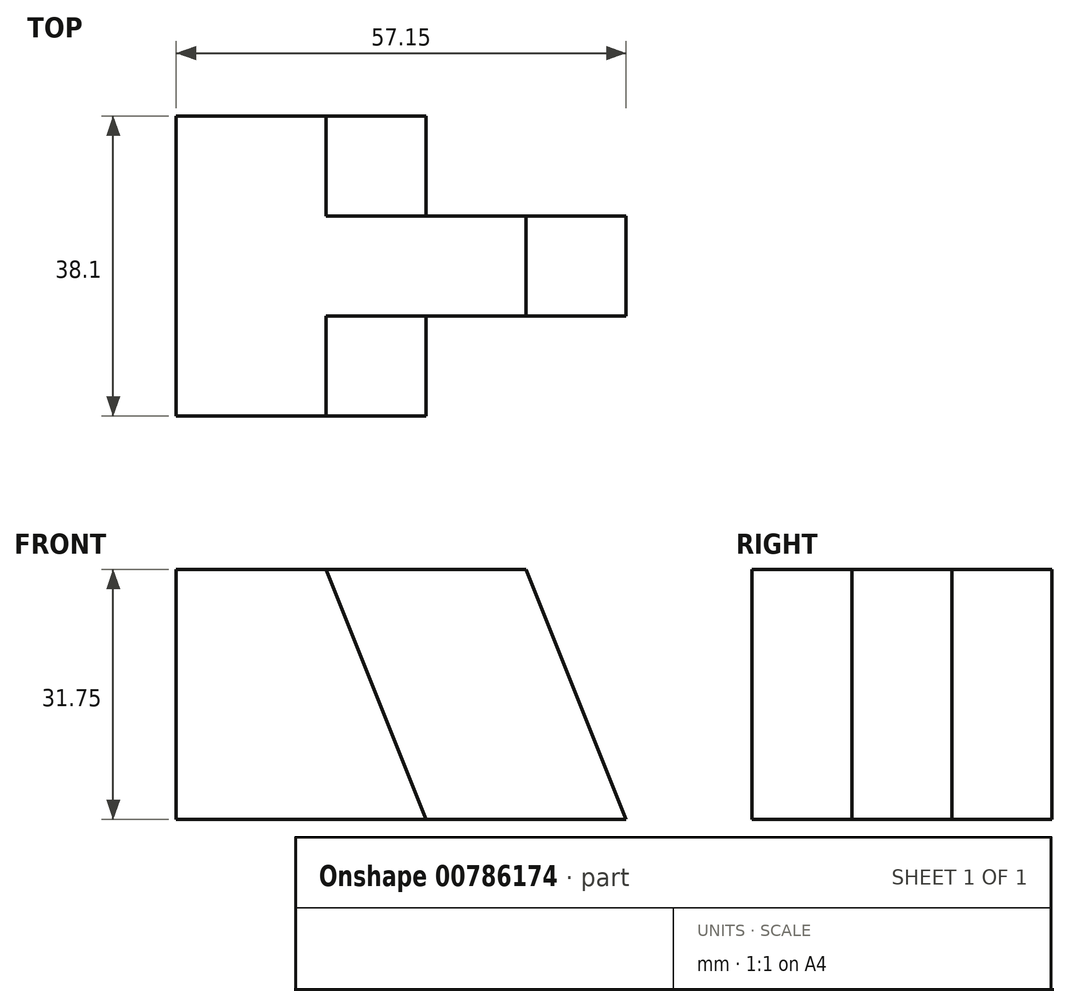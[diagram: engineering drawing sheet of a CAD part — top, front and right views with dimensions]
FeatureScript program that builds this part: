
annotation { "Feature Type Name" : "Feature", "Feature Type Description" : "" }
export const myFeature = defineFeature(function(context is Context, id is Id, definition is map)
    precondition{}
    {
        {
            var Q0;
            Q0=qCreatedBy(makeId("Front.planeOp"),FACE);
            var sketch = newSketch(context, id + "F0", { "sketchPlane" : qUnion([Q0])});
            skLineSegment(sketch, "E0", {"start": v(0, 0) * mm, "end": v(0, 31.75) * mm});
            skLineSegment(sketch, "E1", {"start": v(0, 0) * mm, "end": v(57.15, 0) * mm});
            skLineSegment(sketch, "E2", {"start": v(57.15, 0) * mm, "end": v(57.15, 31.75) * mm});
            skLineSegment(sketch, "E3", {"start": v(57.15, 31.75) * mm, "end": v(0, 31.75) * mm});
            skSolve(sketch);
        }
        {
            var Q0;
            Q0=makeQuery(id+"F0.imprint","IMPRINT",FACE,{"disambiguationData":[TD([[makeQuery(id+"F0.imprint","IMPRINT",EDGE,{"derivedFrom":sQuery(id+"F0.wireOp",EDGE,"E0")}),-1.0]])]});
            extrude(context, id + "F1", {"entities" : qUnion([Q0]), "depth" : 38.1 * mm, "offsetDistance" : 25.4 * mm});
        }
        {
            var Q0;
            Q0=makeQuery(id+"F1.opExtrude","CAP_FACE",FACE,{"disambiguationData":[OSD([sQuery(id+"F0.wireOp",EDGE,"E0"),sQuery(id+"F0.wireOp",EDGE,"E1"),sQuery(id+"F0.wireOp",EDGE,"E2"),sQuery(id+"F0.wireOp",EDGE,"E3")])],"isStart":false});
            var sketch = newSketch(context, id + "F2", { "sketchPlane" : qUnion([Q0])});
            skLineSegment(sketch, "E4", {"start": v(57.15, 31.75) * mm, "end": v(19.05, 31.75) * mm});
            skLineSegment(sketch, "E5", {"start": v(57.15, 31.75) * mm, "end": v(57.15, 0) * mm});
            skLineSegment(sketch, "E6", {"start": v(57.15, 0) * mm, "end": v(31.75, 0) * mm});
            skLineSegment(sketch, "E7", {"start": v(31.75, 0) * mm, "end": v(19.05, 31.75) * mm});
            skSolve(sketch);
        }
        {
            var Q0;
            Q0=makeQuery(id+"F2.imprint","IMPRINT",FACE,{"disambiguationData":[TD([[makeQuery(id+"F2.imprint","IMPRINT",EDGE,{"derivedFrom":sQuery(id+"F2.wireOp",EDGE,"E4")}),1.0]])]});
            extrude(context, id + "F3", {"entities" : qUnion([Q0]), "operationType" : NewBodyOperationType.REMOVE, "oppositeDirection" : true, "depth" : 12.7 * mm, "offsetDistance" : 25.4 * mm});
        }
        {
            var Q0;
            Q0=makeQuery(id+"F1.opExtrude","CAP_FACE",FACE,{"disambiguationData":[OSD([sQuery(id+"F0.wireOp",EDGE,"E0"),sQuery(id+"F0.wireOp",EDGE,"E1"),sQuery(id+"F0.wireOp",EDGE,"E2"),sQuery(id+"F0.wireOp",EDGE,"E3")])],"isStart":true});
            var sketch = newSketch(context, id + "F4", { "sketchPlane" : qUnion([Q0])});
            skLineSegment(sketch, "E8", {"start": v(-57.15, 31.75) * mm, "end": v(-19.05, 31.75) * mm});
            skLineSegment(sketch, "E9", {"start": v(-57.15, 31.75) * mm, "end": v(-57.15, 0) * mm});
            skLineSegment(sketch, "E10", {"start": v(-57.15, 0) * mm, "end": v(-31.75, 0) * mm});
            skLineSegment(sketch, "E11", {"start": v(-31.75, 0) * mm, "end": v(-19.05, 31.75) * mm});
            skSolve(sketch);
        }
        {
            var Q0;
            Q0=makeQuery(id+"F4.imprint","IMPRINT",FACE,{"disambiguationData":[TD([[makeQuery(id+"F4.imprint","IMPRINT",EDGE,{"derivedFrom":sQuery(id+"F4.wireOp",EDGE,"E8")}),-1.0]])]});
            extrude(context, id + "F5", {"entities" : qUnion([Q0]), "operationType" : NewBodyOperationType.REMOVE, "oppositeDirection" : true, "depth" : 12.7 * mm, "offsetDistance" : 25.4 * mm});
        }
        {
            var Q0;
            Q0=makeQuery(id+"F3.boolean.opBoolean","COPY",FACE,{"derivedFrom":makeQuery(id+"F3.opExtrude","CAP_FACE",FACE,{"disambiguationData":[OSD([sQuery(id+"F2.wireOp",EDGE,"E4"),sQuery(id+"F2.wireOp",EDGE,"E5"),sQuery(id+"F2.wireOp",EDGE,"E6"),sQuery(id+"F2.wireOp",EDGE,"E7")])],"isStart":false})});
            var sketch = newSketch(context, id + "F6", { "sketchPlane" : qUnion([Q0])});
            skLineSegment(sketch, "E12", {"start": v(57.15, 0) * mm, "end": v(57.15, 31.75) * mm});
            skLineSegment(sketch, "E13", {"start": v(57.15, 31.75) * mm, "end": v(44.45, 31.75) * mm});
            skLineSegment(sketch, "E14", {"start": v(44.45, 31.75) * mm, "end": v(57.15, 0) * mm});
            skSolve(sketch);
        }
        {
            var Q0;
            Q0=makeQuery(id+"F6.imprint","IMPRINT",FACE,{"disambiguationData":[TD([[makeQuery(id+"F6.imprint","IMPRINT",EDGE,{"derivedFrom":sQuery(id+"F6.wireOp",EDGE,"E12")}),1.0]])]});
            extrude(context, id + "F7", {"entities" : qUnion([Q0]), "operationType" : NewBodyOperationType.REMOVE, "oppositeDirection" : true, "depth" : 12.7 * mm, "offsetDistance" : 25.4 * mm});
        }
    });
